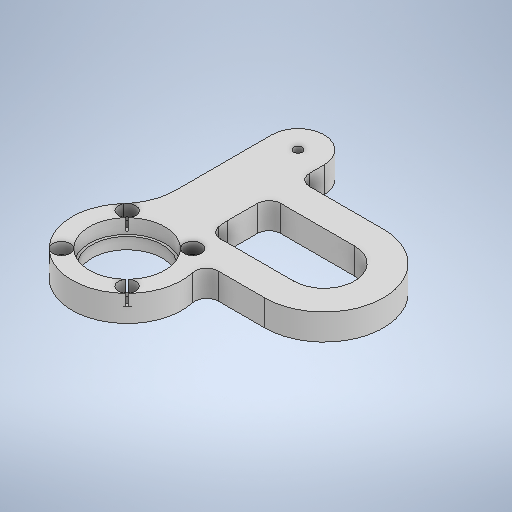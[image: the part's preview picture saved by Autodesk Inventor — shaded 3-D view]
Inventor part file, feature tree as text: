
AUTODESK INVENTOR PART (.ipt)
format: ipt  version: 2025.2 (Build 292293000, 293)  size: 716,800 bytes
history: native  units: mm
features: sketch x6, extrude x5, other x1, fillet x1
ambient origin geometry x8: Origin, YZ Plane, XZ Plane, XY Plane, X Axis, Y Axis, Z Axis, Center Point
bodies: Solid1 (feature_tree)
feature tree (13):
  other  "leg_extend"
  extrude  "Extrusion1"  Depth=29.5mm
  extrude  "Extrusion2"  Depth=18.0mm
  extrude  "Extrusion3"  Depth=19.0mm
  extrude  "Extrusion4"  Depth=9.0mm
  extrude  "Extrusion5"  Depth=3.0mm
  fillet  "Fillet2"  [1 undecoded]
  sketch  "Sketch1"  dims[d0=59.0mm d1=29.5mm]
  sketch  "Sketch2"  dims[d4=19.0mm d5=26.065mm]
  sketch  "Sketch3"  dims[d6=9.0mm d7=0.0mm d8=0.85mm]
  sketch  "Sketch4"  dims[d9=4.0mm d10=0.0mm d11=3.0mm d12=0.0mm d13=0.0mm]
  sketch  "Sketch Circular Pattern1"  dims[d2=38.0mm d3=18.0mm]
  sketch  "Sketch5"  dims[d14=45.0deg d15=3.0mm d16=40.0mm d18=360.0deg d20=0.0mm d21=0.0mm d22=6.0mm d23=6.0mm d24=6.0mm d25=6.0mm d26=4.0mm d27=0.0mm d31=10.0mm d32=59.0mm d33=4.0mm]
note: 1 required parameter value undecoded (feature->parameter linkage not recoverable at this tier; creation-order binding heuristic only, values carry confidence <= 0.55)
